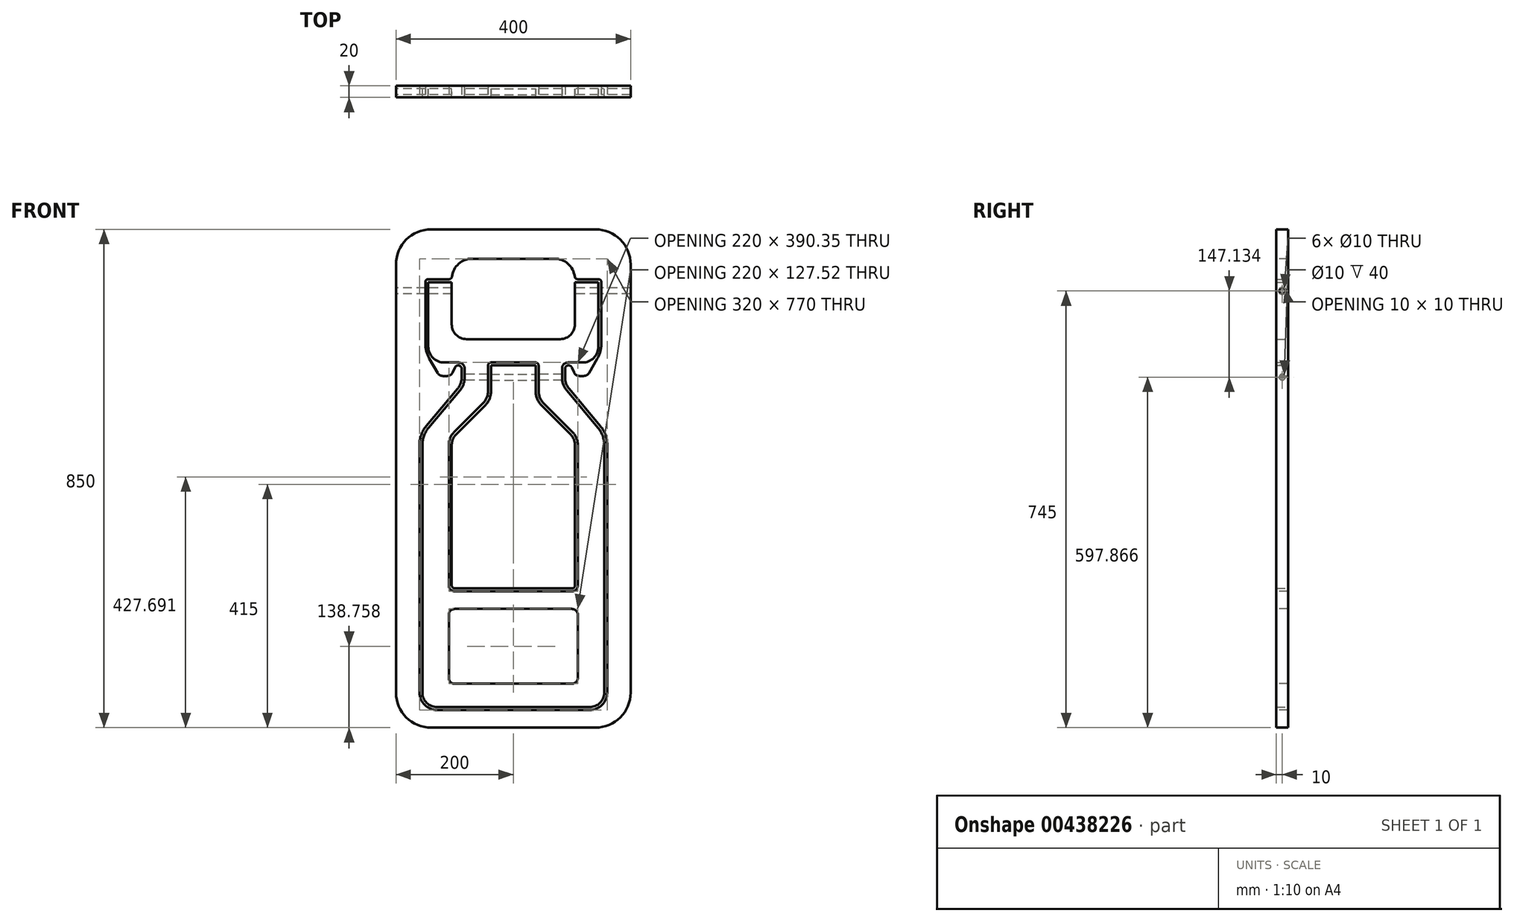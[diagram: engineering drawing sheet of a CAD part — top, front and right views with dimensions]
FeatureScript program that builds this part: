
annotation { "Feature Type Name" : "Feature", "Feature Type Description" : "" }
export const myFeature = defineFeature(function(context is Context, id is Id, definition is map)
    precondition{}
    {
        {
            var Q0;
            Q0=qCreatedBy(makeId("Front.planeOp"),FACE);
            var sketch = newSketch(context, id + "F0", { "sketchPlane" : qUnion([Q0])});
            skLineSegment(sketch, "E0.bottom", {"start": v(-200, 425) * mm, "end": v(200, 425) * mm});
            skLineSegment(sketch, "E0.top", {"start": v(-200, -425) * mm, "end": v(200, -425) * mm});
            skLineSegment(sketch, "E0.left", {"start": v(-200, 425) * mm, "end": v(-200, -425) * mm});
            skLineSegment(sketch, "E0.right", {"start": v(200, 425) * mm, "end": v(200, -425) * mm});
            skLineSegment(sketch, "E1", {"start": v(-200, 425) * mm, "end": v(200, -425) * mm, "construction": true});
            skLineSegment(sketch, "E2", {"start": v(0, 425) * mm, "end": v(0, -425) * mm, "construction": true});
            skSolve(sketch);
        }
        {
            var Q0;
            Q0 = qSketchRegion(id + "F0", true);
            extrude(context, id + "F1", {"entities" : qUnion([Q0]), "depth" : 20 * mm});
        }
        {
            var Q0;
            Q0=makeQuery(id+"F1.opExtrude","SWEPT_EDGE",EDGE,{"disambiguationData":[OSD([sQuery(id+"F0.wireOp",EDGE,"E0.bottom"),sQuery(id+"F0.wireOp",EDGE,"E0.right")])]});
            var Q1;
            Q1=makeQuery(id+"F1.opExtrude","SWEPT_EDGE",EDGE,{"disambiguationData":[OSD([sQuery(id+"F0.wireOp",EDGE,"E0.bottom"),sQuery(id+"F0.wireOp",EDGE,"E0.left")])]});
            var Q2;
            Q2=makeQuery(id+"F1.opExtrude","SWEPT_EDGE",EDGE,{"disambiguationData":[OSD([sQuery(id+"F0.wireOp",EDGE,"E0.top"),sQuery(id+"F0.wireOp",EDGE,"E0.left")])]});
            var Q3;
            Q3=makeQuery(id+"F1.opExtrude","SWEPT_EDGE",EDGE,{"disambiguationData":[OSD([sQuery(id+"F0.wireOp",EDGE,"E0.top"),sQuery(id+"F0.wireOp",EDGE,"E0.right")])]});
            fillet(context, id + "F2", {"entities" : qUnion([Q0, Q1, Q2, Q3]), "radius" : 60 * mm, "tangentPropagation" : true, "allowEdgeOverflow" : false});
        }
        {
            var Q0;
            Q0=makeQuery(id+"F1.opExtrude","CAP_FACE",FACE,{"disambiguationData":[OSD([sQuery(id+"F0.wireOp",EDGE,"E0.bottom"),sQuery(id+"F0.wireOp",EDGE,"E0.top"),sQuery(id+"F0.wireOp",EDGE,"E0.left"),sQuery(id+"F0.wireOp",EDGE,"E0.right")])],"isStart":false});
            var sketch = newSketch(context, id + "F3", { "sketchPlane" : qUnion([Q0])});
            skLineSegment(sketch, "E3", {"start": v(-70, 375) * mm, "end": v(70, 375) * mm});
            skLineSegment(sketch, "E4", {"start": v(0, 0) * mm, "end": v(0, 375) * mm, "construction": true});
            skArc(sketch, "E5", {"start": v(-70, 375) * mm, "mid": v(-94.75, 364.75) * mm, "end": v(-105, 340) * mm});
            skLineSegment(sketch, "E6", {"start": v(-105, 340) * mm, "end": v(-150, 340) * mm});
            skLineSegment(sketch, "E7", {"start": v(-150, 340) * mm, "end": v(-150, 216.43) * mm});
            skLineSegment(sketch, "E8", {"start": v(-150, 216.43) * mm, "end": v(-126.08, 175) * mm});
            skLineSegment(sketch, "E9", {"start": v(-126.08, 175) * mm, "end": v(-106.08, 175) * mm});
            skLineSegment(sketch, "E10", {"start": v(-106.08, 175) * mm, "end": v(-99.55, 189.47) * mm});
            skArc(sketch, "E11", {"start": v(-99.55, 189.47) * mm, "mid": v(-92.82, 192.87) * mm, "end": v(-88.08, 187) * mm});
            skLineSegment(sketch, "E12", {"start": v(-88.08, 161.42) * mm, "end": v(-160, 75.71) * mm});
            skLineSegment(sketch, "E13", {"start": v(-160, 75.71) * mm, "end": v(-160, -365) * mm});
            skLineSegment(sketch, "E14", {"start": v(-130, -395) * mm, "end": v(130, -395) * mm});
            skLineSegment(sketch, "E15.MirrorCS", {"start": v(160, 75.71) * mm, "end": v(160, -365) * mm});
            skLineSegment(sketch, "E16.MirrorCS", {"start": v(88.08, 161.42) * mm, "end": v(160, 75.71) * mm});
            skArc(sketch, "E17.MirrorCS", {"start": v(99.55, 189.47) * mm, "mid": v(92.82, 192.87) * mm, "end": v(88.08, 187) * mm});
            skLineSegment(sketch, "E18.MirrorCS", {"start": v(106.08, 175) * mm, "end": v(99.55, 189.47) * mm});
            skLineSegment(sketch, "E19.MirrorCS", {"start": v(126.08, 175) * mm, "end": v(106.08, 175) * mm});
            skLineSegment(sketch, "E20.MirrorCS", {"start": v(150, 216.43) * mm, "end": v(126.08, 175) * mm});
            skArc(sketch, "E21.MirrorCS", {"start": v(70, 375) * mm, "mid": v(94.75, 364.75) * mm, "end": v(105, 340) * mm});
            skLineSegment(sketch, "E22.MirrorCS", {"start": v(150, 340) * mm, "end": v(150, 216.43) * mm});
            skLineSegment(sketch, "E23.MirrorCS", {"start": v(105, 340) * mm, "end": v(150, 340) * mm});
            skPoint(sketch, "E24.visualSharp", {"position": v(-160, -395) * mm});
            skArc(sketch, "E24.filletArc", {"start": v(-160, -365) * mm, "mid": v(-151.21, -386.21) * mm, "end": v(-130, -395) * mm});
            skPoint(sketch, "E25.visualSharp", {"position": v(160, -395) * mm});
            skArc(sketch, "E25.filletArc", {"start": v(130, -395) * mm, "mid": v(151.21, -386.21) * mm, "end": v(160, -365) * mm});
            skLineSegment(sketch, "E26", {"start": v(-88.08, 161.42) * mm, "end": v(-88.08, 187) * mm});
            skLineSegment(sketch, "E27.MirrorCS", {"start": v(88.08, 161.42) * mm, "end": v(88.08, 187) * mm});
            skSolve(sketch);
        }
        {
            var Q0;
            Q0 = qSketchRegion(id + "F3", true);
            extrude(context, id + "F4", {"entities" : qUnion([Q0]), "operationType" : NewBodyOperationType.REMOVE, "endBound" : BoundingType.THROUGH_ALL, "oppositeDirection" : true, "depth" : 25 * mm});
        }
        {
            var Q0;
            Q0=makeQuery(id+"F4.boolean.opBoolean","COPY",EDGE,{"derivedFrom":makeQuery(id+"F4.opExtrude","SWEPT_EDGE",EDGE,{"disambiguationData":[OSD([sQuery(id+"F3.wireOp",EDGE,"E7"),sQuery(id+"F3.wireOp",EDGE,"E8")])]})});
            var Q1;
            Q1=makeQuery(id+"F4.boolean.opBoolean","COPY",EDGE,{"derivedFrom":makeQuery(id+"F4.opExtrude","SWEPT_EDGE",EDGE,{"disambiguationData":[OSD([sQuery(id+"F3.wireOp",EDGE,"E20.MirrorCS"),sQuery(id+"F3.wireOp",EDGE,"E22.MirrorCS")])]})});
            fillet(context, id + "F5", {"entities" : qUnion([Q0, Q1]), "radius" : 50 * mm, "tangentPropagation" : true, "allowEdgeOverflow" : false});
        }
        {
            var Q0;
            Q0=makeQuery(id+"F4.boolean.opBoolean","COPY",EDGE,{"derivedFrom":makeQuery(id+"F4.opExtrude","SWEPT_EDGE",EDGE,{"disambiguationData":[OSD([sQuery(id+"F3.wireOp",EDGE,"E19.MirrorCS"),sQuery(id+"F3.wireOp",EDGE,"E20.MirrorCS")])]})});
            var Q1;
            Q1=makeQuery(id+"F4.boolean.opBoolean","COPY",EDGE,{"derivedFrom":makeQuery(id+"F4.opExtrude","SWEPT_EDGE",EDGE,{"disambiguationData":[OSD([sQuery(id+"F3.wireOp",EDGE,"E8"),sQuery(id+"F3.wireOp",EDGE,"E9")])]})});
            var Q2;
            Q2=makeQuery(id+"F4.boolean.opBoolean","COPY",EDGE,{"derivedFrom":makeQuery(id+"F4.opExtrude","SWEPT_EDGE",EDGE,{"disambiguationData":[OSD([sQuery(id+"F3.wireOp",EDGE,"E18.MirrorCS"),sQuery(id+"F3.wireOp",EDGE,"E19.MirrorCS")])]})});
            var Q3;
            Q3=makeQuery(id+"F4.boolean.opBoolean","COPY",EDGE,{"derivedFrom":makeQuery(id+"F4.opExtrude","SWEPT_EDGE",EDGE,{"disambiguationData":[OSD([sQuery(id+"F3.wireOp",EDGE,"E9"),sQuery(id+"F3.wireOp",EDGE,"E10")])]})});
            fillet(context, id + "F6", {"entities" : qUnion([Q0, Q1, Q2, Q3]), "radius" : 10 * mm, "tangentPropagation" : true, "allowEdgeOverflow" : false});
        }
        {
            var Q0;
            Q0=makeQuery(id+"F4.boolean.opBoolean","COPY",EDGE,{"derivedFrom":makeQuery(id+"F4.opExtrude","SWEPT_EDGE",EDGE,{"disambiguationData":[OSD([sQuery(id+"F3.wireOp",EDGE,"E12"),sQuery(id+"F3.wireOp",EDGE,"E26")])]})});
            var Q1;
            Q1=makeQuery(id+"F4.boolean.opBoolean","COPY",EDGE,{"derivedFrom":makeQuery(id+"F4.opExtrude","SWEPT_EDGE",EDGE,{"disambiguationData":[OSD([sQuery(id+"F3.wireOp",EDGE,"E16.MirrorCS"),sQuery(id+"F3.wireOp",EDGE,"E27.MirrorCS")])]})});
            fillet(context, id + "F7", {"entities" : qUnion([Q0, Q1]), "radius" : 30 * mm, "tangentPropagation" : true, "allowEdgeOverflow" : false});
        }
        {
            var Q0;
            Q0=makeQuery(id+"F4.boolean.opBoolean","COPY",EDGE,{"derivedFrom":makeQuery(id+"F4.opExtrude","SWEPT_EDGE",EDGE,{"disambiguationData":[OSD([sQuery(id+"F3.wireOp",EDGE,"E12"),sQuery(id+"F3.wireOp",EDGE,"E13")])]})});
            var Q1;
            Q1=makeQuery(id+"F4.boolean.opBoolean","COPY",EDGE,{"derivedFrom":makeQuery(id+"F4.opExtrude","SWEPT_EDGE",EDGE,{"disambiguationData":[OSD([sQuery(id+"F3.wireOp",EDGE,"E15.MirrorCS"),sQuery(id+"F3.wireOp",EDGE,"E16.MirrorCS")])]})});
            fillet(context, id + "F8", {"entities" : qUnion([Q0, Q1]), "radius" : 50 * mm, "tangentPropagation" : true, "allowEdgeOverflow" : false});
        }
        {
            var Q0;
            Q0=makeQuery(id+"F4.boolean.opBoolean","COPY",EDGE,{"derivedFrom":makeQuery(id+"F4.opExtrude","SWEPT_EDGE",EDGE,{"disambiguationData":[OSD([sQuery(id+"F3.wireOp",EDGE,"E6"),sQuery(id+"F3.wireOp",EDGE,"E7")])]})});
            var Q1;
            Q1=makeQuery(id+"F4.boolean.opBoolean","COPY",EDGE,{"derivedFrom":makeQuery(id+"F4.opExtrude","SWEPT_EDGE",EDGE,{"disambiguationData":[OSD([sQuery(id+"F3.wireOp",EDGE,"E5"),sQuery(id+"F3.wireOp",EDGE,"E6")])]})});
            var Q2;
            Q2=makeQuery(id+"F4.boolean.opBoolean","COPY",EDGE,{"derivedFrom":makeQuery(id+"F4.opExtrude","SWEPT_EDGE",EDGE,{"disambiguationData":[OSD([sQuery(id+"F3.wireOp",EDGE,"E22.MirrorCS"),sQuery(id+"F3.wireOp",EDGE,"E23.MirrorCS")])]})});
            var Q3;
            Q3=makeQuery(id+"F4.boolean.opBoolean","COPY",EDGE,{"derivedFrom":makeQuery(id+"F4.opExtrude","SWEPT_EDGE",EDGE,{"disambiguationData":[OSD([sQuery(id+"F3.wireOp",EDGE,"E21.MirrorCS"),sQuery(id+"F3.wireOp",EDGE,"E23.MirrorCS")])]})});
            fillet(context, id + "F9", {"entities" : qUnion([Q0, Q1, Q2, Q3]), "radius" : 5 * mm, "tangentPropagation" : true, "allowEdgeOverflow" : false});
        }
        {
            var Q0;
            Q0=qCreatedBy(makeId("Front.planeOp"),FACE);
            var sketch = newSketch(context, id + "F10", { "sketchPlane" : qUnion([Q0])});
            skLineSegment(sketch, "E28.2", {"start": v(-105, 335) * mm, "end": v(-145, 335) * mm});
            skLineSegment(sketch, "E28.3", {"start": v(-145, 335) * mm, "end": v(-145, 225.05) * mm});
            skArc(sketch, "E28.4", {"start": v(-117.82, 197.87) * mm, "mid": v(-137.04, 205.83) * mm, "end": v(-145, 225.05) * mm});
            skLineSegment(sketch, "E28.12", {"start": v(-83.08, 172.34) * mm, "end": v(-83.08, 187.87) * mm});
            skArc(sketch, "E28.13", {"start": v(-91.27, 149.84) * mm, "mid": v(-85.2, 160.37) * mm, "end": v(-83.08, 172.34) * mm});
            skLineSegment(sketch, "E28.31", {"start": v(-130, -390) * mm, "end": v(0, -390) * mm});
            skArc(sketch, "E28.32", {"start": v(-155, -365) * mm, "mid": v(-147.68, -382.68) * mm, "end": v(-130, -390) * mm});
            skLineSegment(sketch, "E28.33", {"start": v(-155, 57.52) * mm, "end": v(-155, -365) * mm});
            skArc(sketch, "E28.34", {"start": v(-155, 57.52) * mm, "mid": v(-152.29, 72.9) * mm, "end": v(-144.47, 86.44) * mm});
            skLineSegment(sketch, "E28.35", {"start": v(-91.27, 149.84) * mm, "end": v(-144.47, 86.44) * mm});
            skLineSegment(sketch, "E29", {"start": v(-133.54, 340) * mm, "end": v(-70, 340) * mm, "construction": true});
            skArc(sketch, "E30", {"start": v(-70, 375) * mm, "mid": v(-94.75, 364.75) * mm, "end": v(-105, 340) * mm, "construction": true});
            skLineSegment(sketch, "E31", {"start": v(-105, 335) * mm, "end": v(-105, 262.87) * mm});
            skPoint(sketch, "E32", {"position": v(-70, 375) * mm});
            skLineSegment(sketch, "E33", {"start": v(-93.08, 197.87) * mm, "end": v(-117.82, 197.87) * mm});
            skArc(sketch, "E34.filletArc", {"start": v(-83.08, 187.87) * mm, "mid": v(-86.01, 194.94) * mm, "end": v(-93.08, 197.87) * mm});
            skPoint(sketch, "E35", {"position": v(-93.08, 192.92) * mm});
            skLineSegment(sketch, "E36", {"start": v(-155.42, 235.81) * mm, "end": v(-129.25, 190.49) * mm, "construction": true});
            skLineSegment(sketch, "E37", {"start": v(0, 378.24) * mm, "end": v(0, -521.85) * mm, "construction": true});
            skLineSegment(sketch, "E38", {"start": v(-80, 237.87) * mm, "end": v(0, 237.87) * mm});
            skPoint(sketch, "E39.visualSharp", {"position": v(-105, 237.87) * mm});
            skArc(sketch, "E39.filletArc", {"start": v(-105, 262.87) * mm, "mid": v(-97.68, 245.19) * mm, "end": v(-80, 237.87) * mm});
            skLineSegment(sketch, "E40.MirrorCS", {"start": v(83.08, 172.34) * mm, "end": v(83.08, 187.87) * mm});
            skArc(sketch, "E41.MirrorCS", {"start": v(83.08, 187.87) * mm, "mid": v(86.01, 194.94) * mm, "end": v(93.08, 197.87) * mm});
            skLineSegment(sketch, "E42.MirrorCS", {"start": v(93.08, 197.87) * mm, "end": v(117.82, 197.87) * mm});
            skLineSegment(sketch, "E43.MirrorCS", {"start": v(105, 335) * mm, "end": v(145, 335) * mm});
            skLineSegment(sketch, "E44.MirrorCS", {"start": v(133.54, 340) * mm, "end": v(70, 340) * mm, "construction": true});
            skArc(sketch, "E45.MirrorCS", {"start": v(117.82, 197.87) * mm, "mid": v(137.04, 205.83) * mm, "end": v(145, 225.05) * mm});
            skArc(sketch, "E46.MirrorCS", {"start": v(91.27, 149.84) * mm, "mid": v(85.2, 160.37) * mm, "end": v(83.08, 172.34) * mm});
            skLineSegment(sketch, "E47.MirrorCS", {"start": v(91.27, 149.84) * mm, "end": v(144.47, 86.44) * mm});
            skPoint(sketch, "E48.MirrorP", {"position": v(93.08, 192.92) * mm});
            skLineSegment(sketch, "E49.MirrorCS", {"start": v(80, 237.87) * mm, "end": v(0, 237.87) * mm});
            skLineSegment(sketch, "E50.MirrorCS", {"start": v(130, -390) * mm, "end": v(0, -390) * mm});
            skPoint(sketch, "E51.MirrorP", {"position": v(70, 375) * mm});
            skArc(sketch, "E52.MirrorCS", {"start": v(70, 375) * mm, "mid": v(94.75, 364.75) * mm, "end": v(105, 340) * mm, "construction": true});
            skLineSegment(sketch, "E53.MirrorCS", {"start": v(105, 335) * mm, "end": v(105, 262.87) * mm});
            skArc(sketch, "E54.MirrorCS", {"start": v(155, -365) * mm, "mid": v(147.68, -382.68) * mm, "end": v(130, -390) * mm});
            skLineSegment(sketch, "E55.MirrorCS", {"start": v(155, 57.52) * mm, "end": v(155, -365) * mm});
            skLineSegment(sketch, "E56.MirrorCS", {"start": v(145, 335) * mm, "end": v(145, 225.05) * mm});
            skPoint(sketch, "E57.MirrorP", {"position": v(105, 237.87) * mm});
            skArc(sketch, "E58.MirrorCS", {"start": v(105, 262.87) * mm, "mid": v(97.68, 245.19) * mm, "end": v(80, 237.87) * mm});
            skArc(sketch, "E59.MirrorCS", {"start": v(155, 57.52) * mm, "mid": v(152.29, 72.9) * mm, "end": v(144.47, 86.44) * mm});
            skLineSegment(sketch, "E60.MirrorCS", {"start": v(155.42, 235.81) * mm, "end": v(129.25, 190.49) * mm, "construction": true});
            skSolve(sketch);
        }
        {
            var Q0;
            Q0 = qSketchRegion(id + "F10", true);
            extrude(context, id + "F11", {"entities" : qUnion([Q0]), "depth" : 20 * mm});
        }
        {
            var Q0;
            Q0=makeQuery(id+"F11.opExtrude","CAP_FACE",FACE,{"disambiguationData":[OSD([sQuery(id+"F10.wireOp",EDGE,"E28.2"),sQuery(id+"F10.wireOp",EDGE,"E28.3"),sQuery(id+"F10.wireOp",EDGE,"E28.4"),sQuery(id+"F10.wireOp",EDGE,"E28.12"),sQuery(id+"F10.wireOp",EDGE,"E28.13"),sQuery(id+"F10.wireOp",EDGE,"E28.31"),sQuery(id+"F10.wireOp",EDGE,"E28.32"),sQuery(id+"F10.wireOp",EDGE,"E28.33"),sQuery(id+"F10.wireOp",EDGE,"E28.34"),sQuery(id+"F10.wireOp",EDGE,"E28.35"),sQuery(id+"F10.wireOp",EDGE,"E31"),sQuery(id+"F10.wireOp",EDGE,"E33"),sQuery(id+"F10.wireOp",EDGE,"E34.filletArc"),sQuery(id+"F10.wireOp",EDGE,"E38"),sQuery(id+"F10.wireOp",EDGE,"E39.filletArc"),sQuery(id+"F10.wireOp",EDGE,"E40.MirrorCS"),sQuery(id+"F10.wireOp",EDGE,"E41.MirrorCS"),sQuery(id+"F10.wireOp",EDGE,"E42.MirrorCS"),sQuery(id+"F10.wireOp",EDGE,"E43.MirrorCS"),sQuery(id+"F10.wireOp",EDGE,"E45.MirrorCS"),sQuery(id+"F10.wireOp",EDGE,"E46.MirrorCS"),sQuery(id+"F10.wireOp",EDGE,"E47.MirrorCS"),sQuery(id+"F10.wireOp",EDGE,"E49.MirrorCS"),sQuery(id+"F10.wireOp",EDGE,"E50.MirrorCS"),sQuery(id+"F10.wireOp",EDGE,"E53.MirrorCS"),sQuery(id+"F10.wireOp",EDGE,"E54.MirrorCS"),sQuery(id+"F10.wireOp",EDGE,"E55.MirrorCS"),sQuery(id+"F10.wireOp",EDGE,"E56.MirrorCS"),sQuery(id+"F10.wireOp",EDGE,"E58.MirrorCS"),sQuery(id+"F10.wireOp",EDGE,"E59.MirrorCS")])],"isStart":false});
            var sketch = newSketch(context, id + "F12", { "sketchPlane" : qUnion([Q0])});
            skLineSegment(sketch, "E61.bottom", {"start": v(-38.08, 197.87) * mm, "end": v(38.08, 197.87) * mm});
            skLineSegment(sketch, "E61.left", {"start": v(-43.08, 192.87) * mm, "end": v(-43.08, 149.29) * mm});
            skLineSegment(sketch, "E61.right", {"start": v(43.08, 192.87) * mm, "end": v(43.08, 149.29) * mm});
            skLineSegment(sketch, "E62", {"start": v(0, 237.87) * mm, "end": v(0, 197.87) * mm, "construction": true});
            skLineSegment(sketch, "E63", {"start": v(-51.87, 128.07) * mm, "end": v(-101.21, 78.73) * mm});
            skLineSegment(sketch, "E64", {"start": v(-110, 57.52) * mm, "end": v(-110, -182.48) * mm});
            skLineSegment(sketch, "E65", {"start": v(-100, -192.48) * mm, "end": v(0, -192.48) * mm});
            skLineSegment(sketch, "E66.MirrorCS", {"start": v(51.87, 128.07) * mm, "end": v(101.21, 78.73) * mm});
            skLineSegment(sketch, "E67.MirrorCS", {"start": v(110, 57.52) * mm, "end": v(110, -182.48) * mm});
            skLineSegment(sketch, "E68.MirrorCS", {"start": v(100, -192.48) * mm, "end": v(0, -192.48) * mm});
            skArc(sketch, "E69.filletArc", {"start": v(-101.21, 78.73) * mm, "mid": v(-107.72, 69) * mm, "end": v(-110, 57.52) * mm});
            skArc(sketch, "E70.filletArc", {"start": v(110, 57.52) * mm, "mid": v(107.72, 69) * mm, "end": v(101.21, 78.73) * mm});
            skPoint(sketch, "E71.visualSharp", {"position": v(-110, -192.48) * mm});
            skArc(sketch, "E71.filletArc", {"start": v(-110, -182.48) * mm, "mid": v(-107.07, -189.56) * mm, "end": v(-100, -192.48) * mm});
            skPoint(sketch, "E72.visualSharp", {"position": v(110, -192.48) * mm});
            skArc(sketch, "E72.filletArc", {"start": v(100, -192.48) * mm, "mid": v(107.07, -189.56) * mm, "end": v(110, -182.48) * mm});
            skPoint(sketch, "E73.visualSharp", {"position": v(-43.08, 136.86) * mm});
            skArc(sketch, "E73.filletArc", {"start": v(-51.87, 128.07) * mm, "mid": v(-45.37, 137.8) * mm, "end": v(-43.08, 149.29) * mm});
            skPoint(sketch, "E74.visualSharp", {"position": v(43.08, 136.86) * mm});
            skArc(sketch, "E74.filletArc", {"start": v(43.08, 149.29) * mm, "mid": v(45.37, 137.8) * mm, "end": v(51.87, 128.07) * mm});
            skPoint(sketch, "E75.visualSharp", {"position": v(-43.08, 197.87) * mm});
            skArc(sketch, "E75.filletArc", {"start": v(-38.08, 197.87) * mm, "mid": v(-41.62, 196.4) * mm, "end": v(-43.08, 192.87) * mm});
            skPoint(sketch, "E76.visualSharp", {"position": v(43.08, 197.87) * mm});
            skArc(sketch, "E76.filletArc", {"start": v(43.08, 192.87) * mm, "mid": v(41.62, 196.4) * mm, "end": v(38.08, 197.87) * mm});
            skSolve(sketch);
        }
        {
            var Q0;
            Q0 = qSketchRegion(id + "F12", true);
            extrude(context, id + "F13", {"entities" : qUnion([Q0]), "operationType" : NewBodyOperationType.REMOVE, "oppositeDirection" : true, "depth" : 25 * mm});
        }
        {
            var Q0;
            Q0=makeQuery(id+"F11.opExtrude","CAP_FACE",FACE,{"disambiguationData":[OSD([sQuery(id+"F10.wireOp",EDGE,"E28.2"),sQuery(id+"F10.wireOp",EDGE,"E28.3"),sQuery(id+"F10.wireOp",EDGE,"E28.4"),sQuery(id+"F10.wireOp",EDGE,"E28.12"),sQuery(id+"F10.wireOp",EDGE,"E28.13"),sQuery(id+"F10.wireOp",EDGE,"E28.31"),sQuery(id+"F10.wireOp",EDGE,"E28.32"),sQuery(id+"F10.wireOp",EDGE,"E28.33"),sQuery(id+"F10.wireOp",EDGE,"E28.34"),sQuery(id+"F10.wireOp",EDGE,"E28.35"),sQuery(id+"F10.wireOp",EDGE,"E31"),sQuery(id+"F10.wireOp",EDGE,"E33"),sQuery(id+"F10.wireOp",EDGE,"E34.filletArc"),sQuery(id+"F10.wireOp",EDGE,"E38"),sQuery(id+"F10.wireOp",EDGE,"E39.filletArc"),sQuery(id+"F10.wireOp",EDGE,"E40.MirrorCS"),sQuery(id+"F10.wireOp",EDGE,"E41.MirrorCS"),sQuery(id+"F10.wireOp",EDGE,"E42.MirrorCS"),sQuery(id+"F10.wireOp",EDGE,"E43.MirrorCS"),sQuery(id+"F10.wireOp",EDGE,"E45.MirrorCS"),sQuery(id+"F10.wireOp",EDGE,"E46.MirrorCS"),sQuery(id+"F10.wireOp",EDGE,"E47.MirrorCS"),sQuery(id+"F10.wireOp",EDGE,"E49.MirrorCS"),sQuery(id+"F10.wireOp",EDGE,"E50.MirrorCS"),sQuery(id+"F10.wireOp",EDGE,"E53.MirrorCS"),sQuery(id+"F10.wireOp",EDGE,"E54.MirrorCS"),sQuery(id+"F10.wireOp",EDGE,"E55.MirrorCS"),sQuery(id+"F10.wireOp",EDGE,"E56.MirrorCS"),sQuery(id+"F10.wireOp",EDGE,"E58.MirrorCS"),sQuery(id+"F10.wireOp",EDGE,"E59.MirrorCS")])],"isStart":false});
            var sketch = newSketch(context, id + "F14", { "sketchPlane" : qUnion([Q0])});
            skLineSegment(sketch, "E77.bottom", {"start": v(-100, -222.48) * mm, "end": v(100, -222.48) * mm});
            skLineSegment(sketch, "E77.top", {"start": v(-100, -350) * mm, "end": v(100, -350) * mm});
            skLineSegment(sketch, "E77.left", {"start": v(-110, -232.48) * mm, "end": v(-110, -340) * mm});
            skLineSegment(sketch, "E77.right", {"start": v(110, -232.48) * mm, "end": v(110, -340) * mm});
            skLineSegment(sketch, "E78", {"start": v(0, 183.13) * mm, "end": v(0, -632.86) * mm});
            skPoint(sketch, "E79.visualSharp", {"position": v(-110, -222.48) * mm});
            skArc(sketch, "E79.filletArc", {"start": v(-100, -222.48) * mm, "mid": v(-107.07, -225.41) * mm, "end": v(-110, -232.48) * mm});
            skPoint(sketch, "E80.visualSharp", {"position": v(110, -222.48) * mm});
            skArc(sketch, "E80.filletArc", {"start": v(110, -232.48) * mm, "mid": v(107.07, -225.41) * mm, "end": v(100, -222.48) * mm});
            skPoint(sketch, "E81.visualSharp", {"position": v(110, -350) * mm});
            skArc(sketch, "E81.filletArc", {"start": v(100, -350) * mm, "mid": v(107.07, -347.07) * mm, "end": v(110, -340) * mm});
            skPoint(sketch, "E82.visualSharp", {"position": v(-110, -350) * mm});
            skArc(sketch, "E82.filletArc", {"start": v(-110, -340) * mm, "mid": v(-107.07, -347.07) * mm, "end": v(-100, -350) * mm});
            skSolve(sketch);
        }
        {
            var Q0;
            Q0 = qSketchRegion(id + "F14", true);
            extrude(context, id + "F15", {"entities" : qUnion([Q0]), "operationType" : NewBodyOperationType.REMOVE, "endBound" : BoundingType.THROUGH_ALL, "oppositeDirection" : true, "depth" : 25 * mm});
        }
        {
            var Q0;
            Q0=qCreatedBy(makeId("Front.planeOp"),FACE);
            var sketch = newSketch(context, id + "F16", { "sketchPlane" : qUnion([Q0])});
            skArc(sketch, "E83.0", {"start": v(-48.33, 124.54) * mm, "mid": v(-40.75, 135.9) * mm, "end": v(-38.08, 149.29) * mm});
            skLineSegment(sketch, "E83.1", {"start": v(-38.08, 192.87) * mm, "end": v(-38.08, 149.29) * mm});
            skLineSegment(sketch, "E83.2", {"start": v(-38.08, 192.87) * mm, "end": v(38.08, 192.87) * mm});
            skLineSegment(sketch, "E83.3", {"start": v(100, -187.48) * mm, "end": v(-100, -187.48) * mm});
            skArc(sketch, "E83.4", {"start": v(-105, -182.48) * mm, "mid": v(-103.54, -186.02) * mm, "end": v(-100, -187.48) * mm});
            skLineSegment(sketch, "E83.5", {"start": v(-105, 57.52) * mm, "end": v(-105, -182.48) * mm});
            skArc(sketch, "E83.6", {"start": v(-97.68, 75.2) * mm, "mid": v(-103.1, 67.08) * mm, "end": v(-105, 57.52) * mm});
            skArc(sketch, "E83.7", {"start": v(100, -187.48) * mm, "mid": v(103.54, -186.02) * mm, "end": v(105, -182.48) * mm});
            skLineSegment(sketch, "E83.8", {"start": v(105, 57.52) * mm, "end": v(105, -182.48) * mm});
            skArc(sketch, "E83.9", {"start": v(105, 57.52) * mm, "mid": v(103.1, 67.08) * mm, "end": v(97.68, 75.2) * mm});
            skLineSegment(sketch, "E83.10", {"start": v(-48.33, 124.54) * mm, "end": v(-97.68, 75.2) * mm});
            skLineSegment(sketch, "E83.11", {"start": v(48.33, 124.54) * mm, "end": v(97.68, 75.2) * mm});
            skArc(sketch, "E83.12", {"start": v(38.08, 149.29) * mm, "mid": v(40.75, 135.9) * mm, "end": v(48.33, 124.54) * mm});
            skLineSegment(sketch, "E83.13", {"start": v(38.08, 192.87) * mm, "end": v(38.08, 149.29) * mm});
            skSolve(sketch);
        }
        {
            var Q0;
            Q0 = qSketchRegion(id + "F16", true);
            extrude(context, id + "F17", {"entities" : qUnion([Q0]), "depth" : 20 * mm});
        }
        {
            var Q0;
            Q0=makeQuery(id+"F17.opExtrude","SWEPT_FACE",FACE,{"disambiguationData":[OSD([sQuery(id+"F16.wireOp",EDGE,"E83.13")])]});
            var sketch = newSketch(context, id + "F18", { "sketchPlane" : qUnion([Q0])});
            skPoint(sketch, "E84", {"position": v(-10, 172.87) * mm});
            skLineSegment(sketch, "E85", {"start": v(-20, 172.87) * mm, "end": v(0, 172.87) * mm, "construction": true});
            skSolve(sketch);
        }
        {
            var Q0;
            Q0=sQuery(id+"F18.wireOp",VERTEX,"E84");
            var Q1;
            Q1=makeQuery(id+"F17.opExtrude","SWEPT_BODY",BODY,{"disambiguationData":[OSD([sQuery(id+"F16.wireOp",EDGE,"E83.0"),sQuery(id+"F16.wireOp",EDGE,"E83.1"),sQuery(id+"F16.wireOp",EDGE,"E83.2"),sQuery(id+"F16.wireOp",EDGE,"E83.3"),sQuery(id+"F16.wireOp",EDGE,"E83.4"),sQuery(id+"F16.wireOp",EDGE,"E83.5"),sQuery(id+"F16.wireOp",EDGE,"E83.6"),sQuery(id+"F16.wireOp",EDGE,"E83.7"),sQuery(id+"F16.wireOp",EDGE,"E83.8"),sQuery(id+"F16.wireOp",EDGE,"E83.9"),sQuery(id+"F16.wireOp",EDGE,"E83.10"),sQuery(id+"F16.wireOp",EDGE,"E83.11"),sQuery(id+"F16.wireOp",EDGE,"E83.12"),sQuery(id+"F16.wireOp",EDGE,"E83.13")])]});
            hole(context, id + "F19", {"style" : HoleStyle.SIMPLE, "endStyle" : HoleEndStyle.THROUGH, "holeDiameter" : 10 * mm, "isTappedThrough" : true, "tappedDepth" : 12 * mm, "tapClearance" : 3, "locations" : qUnion([Q0]), "scope" : qUnion([Q1])});
        }
        {
            var Q0;
            Q0=makeQuery(id+"F11.opExtrude","SWEPT_FACE",FACE,{"disambiguationData":[OSD([sQuery(id+"F10.wireOp",EDGE,"E28.12")])]});
            var sketch = newSketch(context, id + "F20", { "sketchPlane" : qUnion([Q0])});
            skPoint(sketch, "E86", {"position": v(10, 172.87) * mm});
            skSolve(sketch);
        }
        {
            var Q0;
            Q0=sQuery(id+"F20.wireOp",VERTEX,"E86");
            var Q1;
            Q1=makeQuery(id+"F11.opExtrude","SWEPT_BODY",BODY,{"disambiguationData":[OSD([sQuery(id+"F10.wireOp",EDGE,"E28.2"),sQuery(id+"F10.wireOp",EDGE,"E28.3"),sQuery(id+"F10.wireOp",EDGE,"E28.4"),sQuery(id+"F10.wireOp",EDGE,"E28.12"),sQuery(id+"F10.wireOp",EDGE,"E28.13"),sQuery(id+"F10.wireOp",EDGE,"E28.31"),sQuery(id+"F10.wireOp",EDGE,"E28.32"),sQuery(id+"F10.wireOp",EDGE,"E28.33"),sQuery(id+"F10.wireOp",EDGE,"E28.34"),sQuery(id+"F10.wireOp",EDGE,"E28.35"),sQuery(id+"F10.wireOp",EDGE,"E31"),sQuery(id+"F10.wireOp",EDGE,"E33"),sQuery(id+"F10.wireOp",EDGE,"E34.filletArc"),sQuery(id+"F10.wireOp",EDGE,"E38"),sQuery(id+"F10.wireOp",EDGE,"E39.filletArc"),sQuery(id+"F10.wireOp",EDGE,"E40.MirrorCS"),sQuery(id+"F10.wireOp",EDGE,"E41.MirrorCS"),sQuery(id+"F10.wireOp",EDGE,"E42.MirrorCS"),sQuery(id+"F10.wireOp",EDGE,"E43.MirrorCS"),sQuery(id+"F10.wireOp",EDGE,"E45.MirrorCS"),sQuery(id+"F10.wireOp",EDGE,"E46.MirrorCS"),sQuery(id+"F10.wireOp",EDGE,"E47.MirrorCS"),sQuery(id+"F10.wireOp",EDGE,"E49.MirrorCS"),sQuery(id+"F10.wireOp",EDGE,"E50.MirrorCS"),sQuery(id+"F10.wireOp",EDGE,"E53.MirrorCS"),sQuery(id+"F10.wireOp",EDGE,"E54.MirrorCS"),sQuery(id+"F10.wireOp",EDGE,"E55.MirrorCS"),sQuery(id+"F10.wireOp",EDGE,"E56.MirrorCS"),sQuery(id+"F10.wireOp",EDGE,"E58.MirrorCS"),sQuery(id+"F10.wireOp",EDGE,"E59.MirrorCS")])]});
            hole(context, id + "F21", {"style" : HoleStyle.SIMPLE, "endStyle" : HoleEndStyle.THROUGH, "holeDiameter" : 10 * mm, "isTappedThrough" : true, "tappedDepth" : 12 * mm, "tapClearance" : 3, "locations" : qUnion([Q0]), "scope" : qUnion([Q1])});
        }
        {
            var Q0;
            Q0=makeQuery(id+"F11.opExtrude","SWEPT_FACE",FACE,{"disambiguationData":[OSD([sQuery(id+"F10.wireOp",EDGE,"E28.3")])]});
            var sketch = newSketch(context, id + "F22", { "sketchPlane" : qUnion([Q0])});
            skLineSegment(sketch, "E87", {"start": v(0, 320) * mm, "end": v(20, 320) * mm, "construction": true});
            skPoint(sketch, "E88", {"position": v(10, 320) * mm});
            skSolve(sketch);
        }
        {
            var Q0;
            Q0=sQuery(id+"F22.wireOp",VERTEX,"E88");
            var Q1;
            Q1=makeQuery(id+"F11.opExtrude","SWEPT_BODY",BODY,{"disambiguationData":[OSD([sQuery(id+"F10.wireOp",EDGE,"E28.2"),sQuery(id+"F10.wireOp",EDGE,"E28.3"),sQuery(id+"F10.wireOp",EDGE,"E28.4"),sQuery(id+"F10.wireOp",EDGE,"E28.12"),sQuery(id+"F10.wireOp",EDGE,"E28.13"),sQuery(id+"F10.wireOp",EDGE,"E28.31"),sQuery(id+"F10.wireOp",EDGE,"E28.32"),sQuery(id+"F10.wireOp",EDGE,"E28.33"),sQuery(id+"F10.wireOp",EDGE,"E28.34"),sQuery(id+"F10.wireOp",EDGE,"E28.35"),sQuery(id+"F10.wireOp",EDGE,"E31"),sQuery(id+"F10.wireOp",EDGE,"E33"),sQuery(id+"F10.wireOp",EDGE,"E34.filletArc"),sQuery(id+"F10.wireOp",EDGE,"E38"),sQuery(id+"F10.wireOp",EDGE,"E39.filletArc"),sQuery(id+"F10.wireOp",EDGE,"E40.MirrorCS"),sQuery(id+"F10.wireOp",EDGE,"E41.MirrorCS"),sQuery(id+"F10.wireOp",EDGE,"E42.MirrorCS"),sQuery(id+"F10.wireOp",EDGE,"E43.MirrorCS"),sQuery(id+"F10.wireOp",EDGE,"E45.MirrorCS"),sQuery(id+"F10.wireOp",EDGE,"E46.MirrorCS"),sQuery(id+"F10.wireOp",EDGE,"E47.MirrorCS"),sQuery(id+"F10.wireOp",EDGE,"E49.MirrorCS"),sQuery(id+"F10.wireOp",EDGE,"E50.MirrorCS"),sQuery(id+"F10.wireOp",EDGE,"E53.MirrorCS"),sQuery(id+"F10.wireOp",EDGE,"E54.MirrorCS"),sQuery(id+"F10.wireOp",EDGE,"E55.MirrorCS"),sQuery(id+"F10.wireOp",EDGE,"E56.MirrorCS"),sQuery(id+"F10.wireOp",EDGE,"E58.MirrorCS"),sQuery(id+"F10.wireOp",EDGE,"E59.MirrorCS")])]});
            hole(context, id + "F23", {"style" : HoleStyle.SIMPLE, "endStyle" : HoleEndStyle.THROUGH, "holeDiameter" : 10 * mm, "isTappedThrough" : true, "tappedDepth" : 12 * mm, "tapClearance" : 3, "locations" : qUnion([Q0]), "scope" : qUnion([Q1])});
        }
        {
            var Q0;
            Q0=makeQuery(id+"F1.opExtrude","SWEPT_FACE",FACE,{"disambiguationData":[OSD([sQuery(id+"F0.wireOp",EDGE,"E0.left")])]});
            var sketch = newSketch(context, id + "F24", { "sketchPlane" : qUnion([Q0])});
            skPoint(sketch, "E89", {"position": v(10, 320) * mm});
            skSolve(sketch);
        }
        {
            var Q0;
            Q0=sQuery(id+"F24.wireOp",VERTEX,"E89");
            var Q1;
            Q1=makeQuery(id+"F1.opExtrude","SWEPT_BODY",BODY,{"disambiguationData":[OSD([sQuery(id+"F0.wireOp",EDGE,"E0.bottom"),sQuery(id+"F0.wireOp",EDGE,"E0.top"),sQuery(id+"F0.wireOp",EDGE,"E0.left"),sQuery(id+"F0.wireOp",EDGE,"E0.right")])]});
            hole(context, id + "F25", {"style" : HoleStyle.SIMPLE, "endStyle" : HoleEndStyle.THROUGH, "holeDiameter" : 10 * mm, "isTappedThrough" : true, "tappedDepth" : 12 * mm, "tapClearance" : 3, "locations" : qUnion([Q0]), "scope" : qUnion([Q1])});
        }
    });
